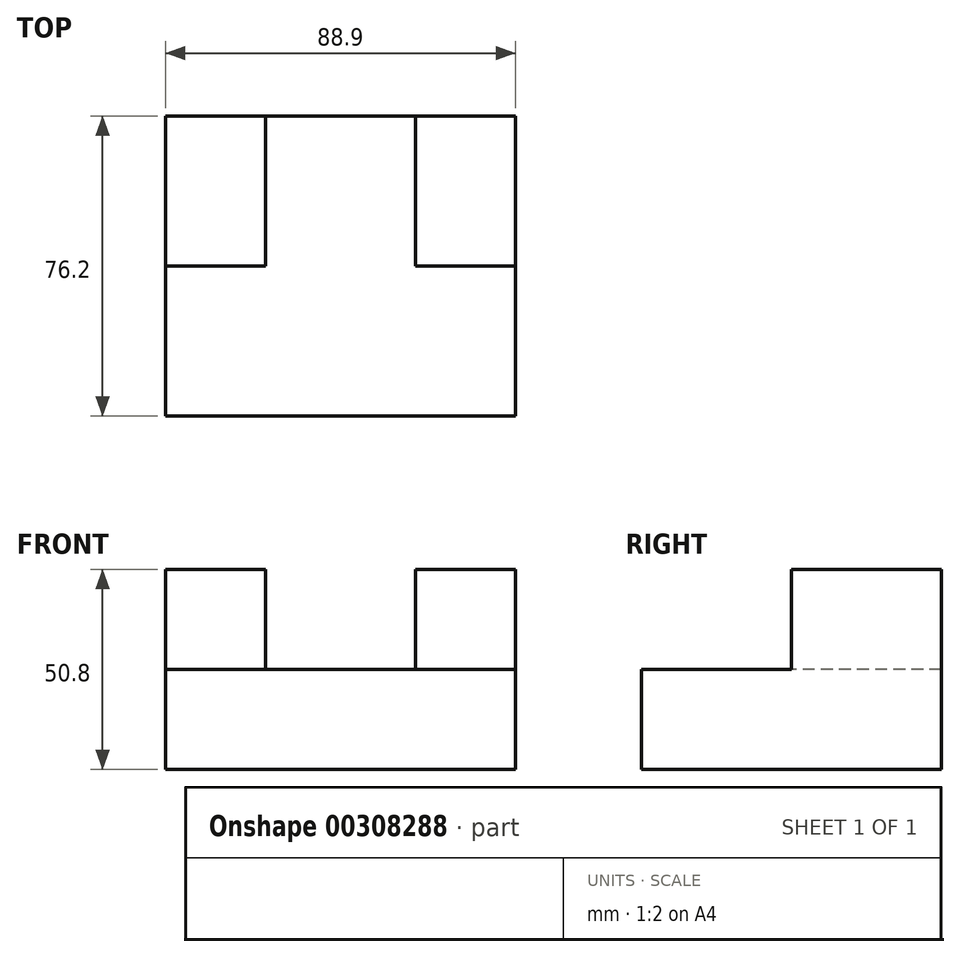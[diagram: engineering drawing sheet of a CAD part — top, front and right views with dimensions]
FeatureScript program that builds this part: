
annotation { "Feature Type Name" : "Feature", "Feature Type Description" : "" }
export const myFeature = defineFeature(function(context is Context, id is Id, definition is map)
    precondition{}
    {
        {
            var Q0;
            Q0=qCreatedBy(makeId("Front.planeOp"),FACE);
            var sketch = newSketch(context, id + "F0", { "sketchPlane" : qUnion([Q0])});
            skLineSegment(sketch, "E0", {"start": v(-44.2, -32.6) * mm, "end": v(-44.2, 18.2) * mm});
            skLineSegment(sketch, "E1", {"start": v(-44.2, 18.2) * mm, "end": v(44.7, 18.2) * mm});
            skLineSegment(sketch, "E2", {"start": v(44.7, 18.2) * mm, "end": v(44.7, -32.6) * mm});
            skLineSegment(sketch, "E3", {"start": v(44.7, -32.6) * mm, "end": v(-44.2, -32.6) * mm});
            skSolve(sketch);
        }
        {
            var Q0;
            Q0 = qSketchRegion(id + "F0", true);
            extrude(context, id + "F1", {"entities" : qUnion([Q0]), "depth" : 76.2 * mm});
        }
        {
            var Q0;
            Q0=makeQuery(id+"F1.opExtrude","SWEPT_FACE",FACE,{"disambiguationData":[OSD([sQuery(id+"F0.wireOp",EDGE,"E1")])]});
            var sketch = newSketch(context, id + "F2", { "sketchPlane" : qUnion([Q0])});
            skLineSegment(sketch, "E4", {"start": v(-18.8, 0) * mm, "end": v(-18.8, -38.1) * mm});
            skLineSegment(sketch, "E5", {"start": v(-18.8, -38.1) * mm, "end": v(-44.2, -38.1) * mm});
            skLineSegment(sketch, "E6", {"start": v(19.3, 0) * mm, "end": v(19.3, -38.1) * mm});
            skLineSegment(sketch, "E7", {"start": v(19.3, -38.1) * mm, "end": v(44.7, -38.1) * mm});
            skLineSegment(sketch, "E8", {"start": v(-18.8, 0) * mm, "end": v(19.3, 0) * mm});
            skSolve(sketch);
        }
        {
            var Q0;
            Q0=makeQuery(id+"F2.imprint","IMPRINT",FACE,{"disambiguationData":[TD([[makeQuery(id+"F2.imprint","IMPRINT",EDGE,{"derivedFrom":sQuery(id+"F2.wireOp",EDGE,"E4")}),1.0]])]});
            extrude(context, id + "F3", {"entities" : qUnion([Q0]), "operationType" : NewBodyOperationType.REMOVE, "oppositeDirection" : true, "depth" : 25.4 * mm});
        }
    });
